# Revit family: UNB_Medical+Care_S4078_BIM_IT
name_source: partatom
category: Plumbing Fixtures
revit_build: Autodesk Revit 2017 (Build: 20160225_1515(x64)
units: mm (PartAtom-declared; Revit-internal decimal feet)

## family parameters
Always vertical = No
Cut with Voids When Loaded = No
OmniClass Number = 23.45.05.21.11.11
OmniClass Title = Water Operated Water Closets
Part Type = Normal
Room Calculation Point = No
Round Connector Dimension = Use Diameter
Shared = No
Work Plane-Based = No

## types (1)
- S4078LJ - CONTOUR 21 SEDILE GRIGIO TOP FIX
    Accessori = www.idealstandard.it
    AltezzaNominale = 61 mm
    Autore = Ideal Standard
    BIMobject category = Toilet Seats
    BIMobject category code = sanitary-toilet-seats
    BIMobject main category = Sanitary
    BIMobject main category code = sanitary
    BOSUseNativeGeometries = 1
    Brand = Ideal Standard
    Brand url = http://www.idealstandard.it
    Caratteristiche = Serie per disabili - Contour 21-Anello in finitura grigia con retaining buffers
    CodiceABarre = 5017830398684
    CodiceDiPrestazione = EN
    Colore = grigio
    Connessione = piombatura
    CostoDiSostituzione = 0 $
    Date of publishing = 2019_01_04
    Description = Serie per disabili - Contour 21-Anello in finitura grigia con retaining buffers
    DescrizioneClassifcazioneUni2015 = WC seats and covers
    Desrizione = Serie per disabili - Contour 21-Anello in finitura grigia con retaining buffers
    Dimensione = 61 x 435 x 375mm
    DimensioneScarico = 0
    EAN code = https://5017830398684
    Edition number = 1
    Finitura = Grigio
    Forma = anello
    Garanzia = Garanzia Ideal Standard
    Grado = n/s
    IFC Classification = IfcFurnitureType
    IfcEsportaCome = USERDEFINED
    InformazioniDiProdotto = http://www.idealstandard.it
    Installation instructions = http://www.idealstandard.it
    Installazione = http://www.idealstandard.it
    InstruzioniInstallazione = http://www.idealstandard.it
    LarghezzaNominale = 375 mm
    LunghezzaNominale = 434 mm
    Maniglia = No
    Manufacturer name = Ideal Standard
    Material main = Plastic
    Materiale = Plastic
    Model = S4078LJ
    ModelloDiRiferimento = Serie per disabili - Contour 21-Anello in finitura grigia con retaining buffers
    NBS Reference Code = 45-35-70/391
    NBS Reference Description = Wc Seats And Covers
    Nome = WcSeatsAndCovers_Contour21_S4078LJ_IdealStandard
    NomeOggettoBim = IS_IdealStandard_WcSeatsAndCovers_Contour21_S4078LJ
    Nominal depth = 0
    Nominal height = 0
    NominalHeight = 61 mm
    NominalLength = 434 mm
    NominalWidth = 375 mm
    NumeroDiModello = S4078LJ
    OmniClass Code = 23-31 19 19 11
    OmniClass Description = Water Operated Water Closets
    PartiDiRicambio = http://www.idealstandard.it
    PesoNetto = 15
    PiattoDoccia = No
    Product Guid = 4bd34fb6-7ab3-4c9b-aabf-6550dd8f67bc
    Product SKU = S4078
    Product certification = http://www.idealstandard.it
    Product data url = https://bimobject.com
    Product family = Sanitary
    Product group = WC Seats and covers
    Product name = MEDCL&CARE SEAT WHITE STD NOCVR TOP FIX
    Product url = http://www.idealstandard.it
    ProfonditaNominale = 0 mm  [stored 0 ft]
    QR code = http://bimobject.com
    Revisione = 1
    RiferimentoClassificazioneUni2015 = Pr_40_20_93_95
    SeatMaterial = 0 mm  [stored 0 ft]
    Size = 61 x 435 x 375mm
    SpessoreDelMateriale = 0
    SpilloverLivello = 0
    Technical description = http://www.idealstandard.it
    Telefono = 800 652 290
    TipoDiDato = Fisso
    TipoEspotazioneIfc = IfcSanitaryTerminalType
    URL = http://www.idealstandard.it
    Uniclass 1.4 Code = L72164
    Uniclass 1.4 Description = WC cisterns
    Uniclass 2.0 Code = PR-35-93-95
    Uniclass 2.0 Description = Wc Seats And Covers
    Uniclass 2015 Code = Pr_40_20_93_95
    Uniclass 2015 Name = WC seats and covers
    UnitàDurata = anni
    UnitàDurataGaranzia = anni
    UnitàLineare = millimetri
    UnitàMonetaria = €
    UnitàSuperficie = €
    UnitàVolume = millimetri
    Versione = 1
    VersioneClassificazioneUni2015 = 1
    Weight Net (Kg) = 0
    Youtube clip = https://www.youtube.com

note: [stored X ft] marks values corroborated as IEEE doubles in the binary element streams (Revit-internal decimal feet)

## geometry (parser evidence)
native form markers: Sweep x2
no freeform markers — native parametric forms only
